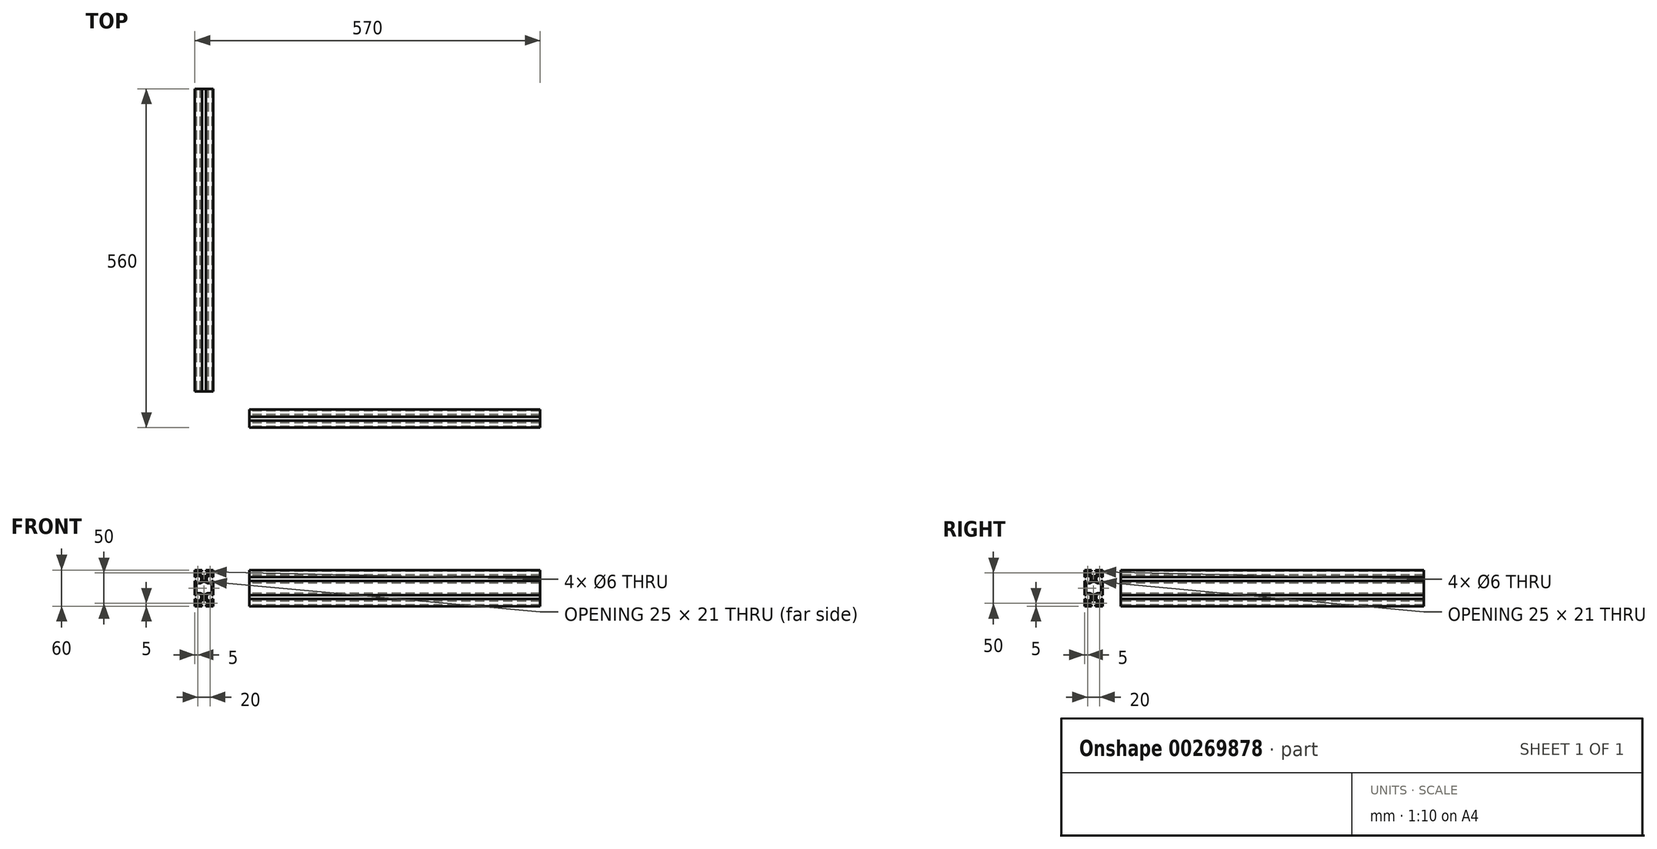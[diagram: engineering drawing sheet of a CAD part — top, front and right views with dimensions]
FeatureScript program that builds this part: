
annotation { "Feature Type Name" : "Feature", "Feature Type Description" : "" }
export const myFeature = defineFeature(function(context is Context, id is Id, definition is map)
    precondition{}
    {
        {
            var Q0;
            Q0=qCreatedBy(makeId("Top.planeOp"),FACE);
            var sketch = newSketch(context, id + "F0", { "sketchPlane" : qUnion([Q0])});
            skCircle(sketch, "E0", {"center": v(0, 0) * mm, "radius": 2.5 * mm});
            skLineSegment(sketch, "E1", {"start": v(0, 0) * mm, "end": v(-15, 0) * mm, "construction": true});
            skLineSegment(sketch, "E2", {"start": v(-15, 0) * mm, "end": v(-15, 15) * mm, "construction": true});
            skLineSegment(sketch, "E3", {"start": v(-15, 15) * mm, "end": v(0, 15) * mm, "construction": true});
            skLineSegment(sketch, "E4", {"start": v(0, 15) * mm, "end": v(0, 0) * mm, "construction": true});
            skLineSegment(sketch, "E5", {"start": v(-15, 15) * mm, "end": v(0, 0) * mm, "construction": true});
            skLineSegment(sketch, "E6", {"start": v(-15, 10) * mm, "end": v(-10, 10) * mm, "construction": true});
            skPoint(sketch, "E7", {"position": v(-15, 3.15) * mm});
            skPoint(sketch, "E8", {"position": v(-15, 5.5) * mm});
            skCircle(sketch, "E9", {"center": v(-10, 10) * mm, "radius": 3 * mm});
            skLineSegment(sketch, "E10", {"start": v(-15, 15) * mm, "end": v(-15, 3.15) * mm});
            skLineSegment(sketch, "E11", {"start": v(-15, 3.15) * mm, "end": v(-12.5, 3.15) * mm});
            skLineSegment(sketch, "E12", {"start": v(-12.5, 3.15) * mm, "end": v(-12.5, 5.5) * mm});
            skPoint(sketch, "E13", {"position": v(-4.5, 0) * mm});
            skLineSegment(sketch, "E14", {"start": v(-12.5, 5.5) * mm, "end": v(-5.5, 5.5) * mm, "construction": true});
            skArc(sketch, "E15", {"start": v(-4.5, 0) * mm, "mid": v(-5.13, 3) * mm, "end": v(-6.9, 5.5) * mm});
            skLineSegment(sketch, "E16", {"start": v(-12.5, 5.5) * mm, "end": v(-6.9, 5.5) * mm});
            skLineSegment(sketch, "E17.0.MirrorCS", {"start": v(-15, 15) * mm, "end": v(-3.15, 15) * mm});
            skPoint(sketch, "E18.visualSharp", {"position": v(-15, 15) * mm});
            skLineSegment(sketch, "E18.filletArc", {"start": v(-15, 15) * mm, "end": v(-15, 15) * mm});
            skLineSegment(sketch, "E19.0.MirrorCS", {"start": v(-3.15, 15) * mm, "end": v(-3.15, 12.5) * mm});
            skLineSegment(sketch, "E20.0.MirrorCS", {"start": v(-3.15, 12.5) * mm, "end": v(-5.5, 12.5) * mm});
            skLineSegment(sketch, "E21.0.MirrorCS", {"start": v(-5.5, 12.5) * mm, "end": v(-5.5, 6.9) * mm});
            skArc(sketch, "E22.0.MirrorCS", {"start": v(0, 4.5) * mm, "mid": v(-3, 5.13) * mm, "end": v(-5.5, 6.9) * mm});
            skArc(sketch, "E23.0.MirrorCS", {"start": v(-4.5, 0) * mm, "mid": v(-5.13, -3) * mm, "end": v(-6.9, -5.5) * mm});
            skLineSegment(sketch, "E24.0.MirrorCS", {"start": v(-12.5, -5.5) * mm, "end": v(-6.9, -5.5) * mm});
            skLineSegment(sketch, "E25.0.MirrorCS", {"start": v(-12.5, -3.15) * mm, "end": v(-12.5, -5.5) * mm});
            skLineSegment(sketch, "E26.0.MirrorCS", {"start": v(-15, -3.15) * mm, "end": v(-12.5, -3.15) * mm});
            skLineSegment(sketch, "E27.0.MirrorCS", {"start": v(-15, -15) * mm, "end": v(-15, -3.15) * mm});
            skLineSegment(sketch, "E28.0.MirrorCS", {"start": v(-15, -15) * mm, "end": v(-15, -15) * mm});
            skLineSegment(sketch, "E29.0.MirrorCS", {"start": v(-15, -15) * mm, "end": v(-3.15, -15) * mm});
            skLineSegment(sketch, "E30.0.MirrorCS", {"start": v(-3.15, -15) * mm, "end": v(-3.15, -12.5) * mm});
            skLineSegment(sketch, "E31.0.MirrorCS", {"start": v(-3.15, -12.5) * mm, "end": v(-5.5, -12.5) * mm});
            skLineSegment(sketch, "E32.0.MirrorCS", {"start": v(-5.5, -12.5) * mm, "end": v(-5.5, -6.9) * mm});
            skArc(sketch, "E33.0.MirrorCS", {"start": v(0, -4.5) * mm, "mid": v(-3, -5.13) * mm, "end": v(-5.5, -6.9) * mm});
            skCircle(sketch, "E34.0.MirrorC", {"center": v(-10, -10) * mm, "radius": 3 * mm});
            skArc(sketch, "E35.0.MirrorCS", {"start": v(0, 4.5) * mm, "mid": v(3, 5.13) * mm, "end": v(5.5, 6.9) * mm});
            skLineSegment(sketch, "E36.0.MirrorCS", {"start": v(5.5, 12.5) * mm, "end": v(5.5, 6.9) * mm});
            skLineSegment(sketch, "E37.0.MirrorCS", {"start": v(3.15, 12.5) * mm, "end": v(5.5, 12.5) * mm});
            skLineSegment(sketch, "E38.0.MirrorCS", {"start": v(3.15, 15) * mm, "end": v(3.15, 12.5) * mm});
            skArc(sketch, "E39.0.MirrorCS", {"start": v(0, -4.5) * mm, "mid": v(3, -5.13) * mm, "end": v(5.5, -6.9) * mm});
            skLineSegment(sketch, "E40.0.MirrorCS", {"start": v(5.5, -12.5) * mm, "end": v(5.5, -6.9) * mm});
            skLineSegment(sketch, "E41.0.MirrorCS", {"start": v(3.15, -12.5) * mm, "end": v(5.5, -12.5) * mm});
            skLineSegment(sketch, "E42.0.MirrorCS", {"start": v(3.15, -15) * mm, "end": v(3.15, -12.5) * mm});
            skLineSegment(sketch, "E43", {"start": v(0, 0) * mm, "end": v(30, 0) * mm, "construction": true});
            skPoint(sketch, "E44", {"position": v(15, 0) * mm});
            skLineSegment(sketch, "E45", {"start": v(15, 15) * mm, "end": v(15, -15) * mm, "construction": true});
            skCircle(sketch, "E46.0.MirrorC", {"center": v(30, 0) * mm, "radius": 2.5 * mm});
            skLineSegment(sketch, "E47.0.MirrorCS", {"start": v(26.85, 15) * mm, "end": v(26.85, 12.5) * mm});
            skLineSegment(sketch, "E48.0.MirrorCS", {"start": v(26.85, 12.5) * mm, "end": v(24.5, 12.5) * mm});
            skLineSegment(sketch, "E49.0.MirrorCS", {"start": v(24.5, 12.5) * mm, "end": v(24.5, 6.9) * mm});
            skArc(sketch, "E50.0.MirrorCS", {"start": v(30, 4.5) * mm, "mid": v(27, 5.13) * mm, "end": v(24.5, 6.9) * mm});
            skArc(sketch, "E51.0.MirrorCS", {"start": v(30, 4.5) * mm, "mid": v(33, 5.13) * mm, "end": v(35.5, 6.9) * mm});
            skLineSegment(sketch, "E52.0.MirrorCS", {"start": v(35.5, 12.5) * mm, "end": v(35.5, 6.9) * mm});
            skLineSegment(sketch, "E53.0.MirrorCS", {"start": v(33.15, 12.5) * mm, "end": v(35.5, 12.5) * mm});
            skLineSegment(sketch, "E54.0.MirrorCS", {"start": v(33.15, 15) * mm, "end": v(33.15, 12.5) * mm});
            skLineSegment(sketch, "E55.0.MirrorCS", {"start": v(45, 15) * mm, "end": v(33.15, 15) * mm});
            skLineSegment(sketch, "E56.0.MirrorCS", {"start": v(45, 15) * mm, "end": v(45, 15) * mm});
            skLineSegment(sketch, "E57.0.MirrorCS", {"start": v(45, 15) * mm, "end": v(45, 3.15) * mm});
            skLineSegment(sketch, "E58.0.MirrorCS", {"start": v(45, 3.15) * mm, "end": v(42.5, 3.15) * mm});
            skLineSegment(sketch, "E59.0.MirrorCS", {"start": v(42.5, 3.15) * mm, "end": v(42.5, 5.5) * mm});
            skLineSegment(sketch, "E60.0.MirrorCS", {"start": v(42.5, 5.5) * mm, "end": v(36.9, 5.5) * mm});
            skArc(sketch, "E61.0.MirrorCS", {"start": v(34.5, 0) * mm, "mid": v(35.13, 3) * mm, "end": v(36.9, 5.5) * mm});
            skArc(sketch, "E62.0.MirrorCS", {"start": v(34.5, 0) * mm, "mid": v(35.13, -3) * mm, "end": v(36.9, -5.5) * mm});
            skLineSegment(sketch, "E63.0.MirrorCS", {"start": v(42.5, -5.5) * mm, "end": v(36.9, -5.5) * mm});
            skLineSegment(sketch, "E64.0.MirrorCS", {"start": v(42.5, -3.15) * mm, "end": v(42.5, -5.5) * mm});
            skLineSegment(sketch, "E65.0.MirrorCS", {"start": v(45, -3.15) * mm, "end": v(42.5, -3.15) * mm});
            skLineSegment(sketch, "E66.0.MirrorCS", {"start": v(45, -15) * mm, "end": v(45, -3.15) * mm});
            skLineSegment(sketch, "E67.0.MirrorCS", {"start": v(45, -15) * mm, "end": v(45, -15) * mm});
            skLineSegment(sketch, "E68.0.MirrorCS", {"start": v(45, -15) * mm, "end": v(33.15, -15) * mm});
            skLineSegment(sketch, "E69.0.MirrorCS", {"start": v(33.15, -15) * mm, "end": v(33.15, -12.5) * mm});
            skLineSegment(sketch, "E70.0.MirrorCS", {"start": v(33.15, -12.5) * mm, "end": v(35.5, -12.5) * mm});
            skLineSegment(sketch, "E71.0.MirrorCS", {"start": v(35.5, -12.5) * mm, "end": v(35.5, -6.9) * mm});
            skArc(sketch, "E72.0.MirrorCS", {"start": v(30, -4.5) * mm, "mid": v(33, -5.13) * mm, "end": v(35.5, -6.9) * mm});
            skArc(sketch, "E73.0.MirrorCS", {"start": v(30, -4.5) * mm, "mid": v(27, -5.13) * mm, "end": v(24.5, -6.9) * mm});
            skLineSegment(sketch, "E74.0.MirrorCS", {"start": v(24.5, -12.5) * mm, "end": v(24.5, -6.9) * mm});
            skLineSegment(sketch, "E75.0.MirrorCS", {"start": v(26.85, -12.5) * mm, "end": v(24.5, -12.5) * mm});
            skLineSegment(sketch, "E76.0.MirrorCS", {"start": v(26.85, -15) * mm, "end": v(26.85, -12.5) * mm});
            skCircle(sketch, "E77.0.MirrorC", {"center": v(40, -10) * mm, "radius": 3 * mm});
            skCircle(sketch, "E78.0.MirrorC", {"center": v(40, 10) * mm, "radius": 3 * mm});
            skLineSegment(sketch, "E79", {"start": v(3.15, 15) * mm, "end": v(26.85, 15) * mm});
            skLineSegment(sketch, "E80", {"start": v(3.15, -15) * mm, "end": v(26.85, -15) * mm});
            skLineSegment(sketch, "E81.0.MirrorCS", {"start": v(0, 15) * mm, "end": v(0, 30) * mm, "construction": true});
            skArc(sketch, "E82.0.MirrorCS", {"start": v(4.5, 0) * mm, "mid": v(5.05, 2.82) * mm, "end": v(6.62, 5.22) * mm});
            skLineSegment(sketch, "E83", {"start": v(6.9, 5.92) * mm, "end": v(6.9, 11.5) * mm});
            skLineSegment(sketch, "E84", {"start": v(7.9, 12.5) * mm, "end": v(15, 12.5) * mm});
            skPoint(sketch, "E85.visualSharp", {"position": v(6.9, 5.5) * mm});
            skArc(sketch, "E85.filletArc", {"start": v(6.62, 5.22) * mm, "mid": v(6.83, 5.54) * mm, "end": v(6.9, 5.92) * mm});
            skPoint(sketch, "E86.visualSharp", {"position": v(6.9, 12.5) * mm});
            skArc(sketch, "E86.filletArc", {"start": v(7.9, 12.5) * mm, "mid": v(7.2, 12.2) * mm, "end": v(6.9, 11.5) * mm});
            skPoint(sketch, "E87", {"position": v(15, 12.5) * mm});
            skLineSegment(sketch, "E88.0.MirrorCS", {"start": v(22.1, 12.5) * mm, "end": v(15, 12.5) * mm});
            skArc(sketch, "E89.0.MirrorCS", {"start": v(22.1, 12.5) * mm, "mid": v(22.8, 12.2) * mm, "end": v(23.1, 11.5) * mm});
            skLineSegment(sketch, "E90.0.MirrorCS", {"start": v(23.1, 5.92) * mm, "end": v(23.1, 11.5) * mm});
            skArc(sketch, "E91.0.MirrorCS", {"start": v(23.38, 5.22) * mm, "mid": v(23.17, 5.54) * mm, "end": v(23.1, 5.92) * mm});
            skArc(sketch, "E92.0.MirrorCS", {"start": v(25.5, 0) * mm, "mid": v(24.95, 2.82) * mm, "end": v(23.38, 5.22) * mm});
            skArc(sketch, "E93.0.MirrorCS", {"start": v(4.5, 0) * mm, "mid": v(5.05, -2.82) * mm, "end": v(6.62, -5.22) * mm});
            skPoint(sketch, "E94.0.MirrorP", {"position": v(6.9, -5.5) * mm});
            skArc(sketch, "E95.0.MirrorCS", {"start": v(6.62, -5.22) * mm, "mid": v(6.83, -5.54) * mm, "end": v(6.9, -5.92) * mm});
            skLineSegment(sketch, "E96.0.MirrorCS", {"start": v(6.9, -5.92) * mm, "end": v(6.9, -11.5) * mm});
            skLineSegment(sketch, "E97.0.MirrorCS", {"start": v(7.9, -12.5) * mm, "end": v(15, -12.5) * mm});
            skArc(sketch, "E98.0.MirrorCS", {"start": v(7.9, -12.5) * mm, "mid": v(7.2, -12.2) * mm, "end": v(6.9, -11.5) * mm});
            skLineSegment(sketch, "E99.0.MirrorCS", {"start": v(22.1, -12.5) * mm, "end": v(15, -12.5) * mm});
            skArc(sketch, "E100.0.MirrorCS", {"start": v(22.1, -12.5) * mm, "mid": v(22.8, -12.2) * mm, "end": v(23.1, -11.5) * mm});
            skLineSegment(sketch, "E101.0.MirrorCS", {"start": v(23.1, -5.92) * mm, "end": v(23.1, -11.5) * mm});
            skArc(sketch, "E102.0.MirrorCS", {"start": v(23.38, -5.22) * mm, "mid": v(23.17, -5.54) * mm, "end": v(23.1, -5.92) * mm});
            skArc(sketch, "E103.0.MirrorCS", {"start": v(25.5, 0) * mm, "mid": v(24.95, -2.82) * mm, "end": v(23.38, -5.22) * mm});
            skSolve(sketch);
        }
        {
            var Q0;
            Q0=qSketchRegion(id+"F0",true);
            extrude(context, id + "F1", {"entities" : qUnion([Q0]), "depth" : 500 * mm});
        }
        {
            var Q0;
            Q0=qSketchRegion(id+"F0",true);
            extrude(context, id + "F2", {"entities" : qUnion([Q0]), "depth" : 480 * mm});
        }
        {
            var Q0;
            Q0=makeQuery(id+"F2.opExtrude","SWEPT_BODY",BODY,{"disambiguationData":[OSD([sQuery(id+"F0.wireOp",EDGE,"E0"),sQuery(id+"F0.wireOp",EDGE,"E9"),sQuery(id+"F0.wireOp",EDGE,"E10"),sQuery(id+"F0.wireOp",EDGE,"E11"),sQuery(id+"F0.wireOp",EDGE,"E12"),sQuery(id+"F0.wireOp",EDGE,"E15"),sQuery(id+"F0.wireOp",EDGE,"E16"),sQuery(id+"F0.wireOp",EDGE,"E17.0.MirrorCS"),sQuery(id+"F0.wireOp",EDGE,"E19.0.MirrorCS"),sQuery(id+"F0.wireOp",EDGE,"E20.0.MirrorCS"),sQuery(id+"F0.wireOp",EDGE,"E21.0.MirrorCS"),sQuery(id+"F0.wireOp",EDGE,"E22.0.MirrorCS"),sQuery(id+"F0.wireOp",EDGE,"E23.0.MirrorCS"),sQuery(id+"F0.wireOp",EDGE,"E24.0.MirrorCS"),sQuery(id+"F0.wireOp",EDGE,"E25.0.MirrorCS"),sQuery(id+"F0.wireOp",EDGE,"E26.0.MirrorCS"),sQuery(id+"F0.wireOp",EDGE,"E27.0.MirrorCS"),sQuery(id+"F0.wireOp",EDGE,"E29.0.MirrorCS"),sQuery(id+"F0.wireOp",EDGE,"E30.0.MirrorCS"),sQuery(id+"F0.wireOp",EDGE,"E31.0.MirrorCS"),sQuery(id+"F0.wireOp",EDGE,"E32.0.MirrorCS"),sQuery(id+"F0.wireOp",EDGE,"E33.0.MirrorCS"),sQuery(id+"F0.wireOp",EDGE,"E34.0.MirrorC"),sQuery(id+"F0.wireOp",EDGE,"E35.0.MirrorCS"),sQuery(id+"F0.wireOp",EDGE,"E36.0.MirrorCS"),sQuery(id+"F0.wireOp",EDGE,"E37.0.MirrorCS"),sQuery(id+"F0.wireOp",EDGE,"E38.0.MirrorCS"),sQuery(id+"F0.wireOp",EDGE,"E39.0.MirrorCS"),sQuery(id+"F0.wireOp",EDGE,"E40.0.MirrorCS"),sQuery(id+"F0.wireOp",EDGE,"E41.0.MirrorCS"),sQuery(id+"F0.wireOp",EDGE,"E42.0.MirrorCS"),sQuery(id+"F0.wireOp",EDGE,"E46.0.MirrorC"),sQuery(id+"F0.wireOp",EDGE,"E47.0.MirrorCS"),sQuery(id+"F0.wireOp",EDGE,"E48.0.MirrorCS"),sQuery(id+"F0.wireOp",EDGE,"E49.0.MirrorCS"),sQuery(id+"F0.wireOp",EDGE,"E50.0.MirrorCS"),sQuery(id+"F0.wireOp",EDGE,"E51.0.MirrorCS"),sQuery(id+"F0.wireOp",EDGE,"E52.0.MirrorCS"),sQuery(id+"F0.wireOp",EDGE,"E53.0.MirrorCS"),sQuery(id+"F0.wireOp",EDGE,"E54.0.MirrorCS"),sQuery(id+"F0.wireOp",EDGE,"E55.0.MirrorCS"),sQuery(id+"F0.wireOp",EDGE,"E57.0.MirrorCS"),sQuery(id+"F0.wireOp",EDGE,"E58.0.MirrorCS"),sQuery(id+"F0.wireOp",EDGE,"E59.0.MirrorCS"),sQuery(id+"F0.wireOp",EDGE,"E60.0.MirrorCS"),sQuery(id+"F0.wireOp",EDGE,"E61.0.MirrorCS"),sQuery(id+"F0.wireOp",EDGE,"E62.0.MirrorCS"),sQuery(id+"F0.wireOp",EDGE,"E63.0.MirrorCS"),sQuery(id+"F0.wireOp",EDGE,"E64.0.MirrorCS"),sQuery(id+"F0.wireOp",EDGE,"E65.0.MirrorCS"),sQuery(id+"F0.wireOp",EDGE,"E66.0.MirrorCS"),sQuery(id+"F0.wireOp",EDGE,"E68.0.MirrorCS"),sQuery(id+"F0.wireOp",EDGE,"E69.0.MirrorCS"),sQuery(id+"F0.wireOp",EDGE,"E70.0.MirrorCS"),sQuery(id+"F0.wireOp",EDGE,"E71.0.MirrorCS"),sQuery(id+"F0.wireOp",EDGE,"E72.0.MirrorCS"),sQuery(id+"F0.wireOp",EDGE,"E73.0.MirrorCS"),sQuery(id+"F0.wireOp",EDGE,"E74.0.MirrorCS"),sQuery(id+"F0.wireOp",EDGE,"E75.0.MirrorCS"),sQuery(id+"F0.wireOp",EDGE,"E76.0.MirrorCS"),sQuery(id+"F0.wireOp",EDGE,"E77.0.MirrorC"),sQuery(id+"F0.wireOp",EDGE,"E78.0.MirrorC"),sQuery(id+"F0.wireOp",EDGE,"E79"),sQuery(id+"F0.wireOp",EDGE,"E80"),sQuery(id+"F0.wireOp",EDGE,"E82.0.MirrorCS"),sQuery(id+"F0.wireOp",EDGE,"E83"),sQuery(id+"F0.wireOp",EDGE,"E84"),sQuery(id+"F0.wireOp",EDGE,"E85.filletArc"),sQuery(id+"F0.wireOp",EDGE,"E86.filletArc"),sQuery(id+"F0.wireOp",EDGE,"E88.0.MirrorCS"),sQuery(id+"F0.wireOp",EDGE,"E89.0.MirrorCS"),sQuery(id+"F0.wireOp",EDGE,"E90.0.MirrorCS"),sQuery(id+"F0.wireOp",EDGE,"E91.0.MirrorCS"),sQuery(id+"F0.wireOp",EDGE,"E92.0.MirrorCS"),sQuery(id+"F0.wireOp",EDGE,"E93.0.MirrorCS"),sQuery(id+"F0.wireOp",EDGE,"E95.0.MirrorCS"),sQuery(id+"F0.wireOp",EDGE,"E96.0.MirrorCS"),sQuery(id+"F0.wireOp",EDGE,"E97.0.MirrorCS"),sQuery(id+"F0.wireOp",EDGE,"E98.0.MirrorCS"),sQuery(id+"F0.wireOp",EDGE,"E99.0.MirrorCS"),sQuery(id+"F0.wireOp",EDGE,"E100.0.MirrorCS"),sQuery(id+"F0.wireOp",EDGE,"E101.0.MirrorCS"),sQuery(id+"F0.wireOp",EDGE,"E102.0.MirrorCS"),sQuery(id+"F0.wireOp",EDGE,"E103.0.MirrorCS")])]});
            var Q1;
            Q1=makeQuery(id+"F1.opExtrude","CAP_EDGE",EDGE,{"disambiguationData":[OSD([sQuery(id+"F0.wireOp",EDGE,"E66.0.MirrorCS")])],"isStart":true});
            transform(context, id + "F3", {"entities" : qUnion([Q0]), "transformType" : TransformType.ROTATION, "transformAxis" : qUnion([Q1]), "angle" : 90 * degree, "makeCopy" : false});
        }
        {
            var Q0;
            Q0=makeQuery(id+"F1.opExtrude","SWEPT_BODY",BODY,{"disambiguationData":[OSD([sQuery(id+"F0.wireOp",EDGE,"E0"),sQuery(id+"F0.wireOp",EDGE,"E9"),sQuery(id+"F0.wireOp",EDGE,"E10"),sQuery(id+"F0.wireOp",EDGE,"E11"),sQuery(id+"F0.wireOp",EDGE,"E12"),sQuery(id+"F0.wireOp",EDGE,"E15"),sQuery(id+"F0.wireOp",EDGE,"E16"),sQuery(id+"F0.wireOp",EDGE,"E17.0.MirrorCS"),sQuery(id+"F0.wireOp",EDGE,"E19.0.MirrorCS"),sQuery(id+"F0.wireOp",EDGE,"E20.0.MirrorCS"),sQuery(id+"F0.wireOp",EDGE,"E21.0.MirrorCS"),sQuery(id+"F0.wireOp",EDGE,"E22.0.MirrorCS"),sQuery(id+"F0.wireOp",EDGE,"E23.0.MirrorCS"),sQuery(id+"F0.wireOp",EDGE,"E24.0.MirrorCS"),sQuery(id+"F0.wireOp",EDGE,"E25.0.MirrorCS"),sQuery(id+"F0.wireOp",EDGE,"E26.0.MirrorCS"),sQuery(id+"F0.wireOp",EDGE,"E27.0.MirrorCS"),sQuery(id+"F0.wireOp",EDGE,"E29.0.MirrorCS"),sQuery(id+"F0.wireOp",EDGE,"E30.0.MirrorCS"),sQuery(id+"F0.wireOp",EDGE,"E31.0.MirrorCS"),sQuery(id+"F0.wireOp",EDGE,"E32.0.MirrorCS"),sQuery(id+"F0.wireOp",EDGE,"E33.0.MirrorCS"),sQuery(id+"F0.wireOp",EDGE,"E34.0.MirrorC"),sQuery(id+"F0.wireOp",EDGE,"E35.0.MirrorCS"),sQuery(id+"F0.wireOp",EDGE,"E36.0.MirrorCS"),sQuery(id+"F0.wireOp",EDGE,"E37.0.MirrorCS"),sQuery(id+"F0.wireOp",EDGE,"E38.0.MirrorCS"),sQuery(id+"F0.wireOp",EDGE,"E39.0.MirrorCS"),sQuery(id+"F0.wireOp",EDGE,"E40.0.MirrorCS"),sQuery(id+"F0.wireOp",EDGE,"E41.0.MirrorCS"),sQuery(id+"F0.wireOp",EDGE,"E42.0.MirrorCS"),sQuery(id+"F0.wireOp",EDGE,"E46.0.MirrorC"),sQuery(id+"F0.wireOp",EDGE,"E47.0.MirrorCS"),sQuery(id+"F0.wireOp",EDGE,"E48.0.MirrorCS"),sQuery(id+"F0.wireOp",EDGE,"E49.0.MirrorCS"),sQuery(id+"F0.wireOp",EDGE,"E50.0.MirrorCS"),sQuery(id+"F0.wireOp",EDGE,"E51.0.MirrorCS"),sQuery(id+"F0.wireOp",EDGE,"E52.0.MirrorCS"),sQuery(id+"F0.wireOp",EDGE,"E53.0.MirrorCS"),sQuery(id+"F0.wireOp",EDGE,"E54.0.MirrorCS"),sQuery(id+"F0.wireOp",EDGE,"E55.0.MirrorCS"),sQuery(id+"F0.wireOp",EDGE,"E57.0.MirrorCS"),sQuery(id+"F0.wireOp",EDGE,"E58.0.MirrorCS"),sQuery(id+"F0.wireOp",EDGE,"E59.0.MirrorCS"),sQuery(id+"F0.wireOp",EDGE,"E60.0.MirrorCS"),sQuery(id+"F0.wireOp",EDGE,"E61.0.MirrorCS"),sQuery(id+"F0.wireOp",EDGE,"E62.0.MirrorCS"),sQuery(id+"F0.wireOp",EDGE,"E63.0.MirrorCS"),sQuery(id+"F0.wireOp",EDGE,"E64.0.MirrorCS"),sQuery(id+"F0.wireOp",EDGE,"E65.0.MirrorCS"),sQuery(id+"F0.wireOp",EDGE,"E66.0.MirrorCS"),sQuery(id+"F0.wireOp",EDGE,"E68.0.MirrorCS"),sQuery(id+"F0.wireOp",EDGE,"E69.0.MirrorCS"),sQuery(id+"F0.wireOp",EDGE,"E70.0.MirrorCS"),sQuery(id+"F0.wireOp",EDGE,"E71.0.MirrorCS"),sQuery(id+"F0.wireOp",EDGE,"E72.0.MirrorCS"),sQuery(id+"F0.wireOp",EDGE,"E73.0.MirrorCS"),sQuery(id+"F0.wireOp",EDGE,"E74.0.MirrorCS"),sQuery(id+"F0.wireOp",EDGE,"E75.0.MirrorCS"),sQuery(id+"F0.wireOp",EDGE,"E76.0.MirrorCS"),sQuery(id+"F0.wireOp",EDGE,"E77.0.MirrorC"),sQuery(id+"F0.wireOp",EDGE,"E78.0.MirrorC"),sQuery(id+"F0.wireOp",EDGE,"E79"),sQuery(id+"F0.wireOp",EDGE,"E80"),sQuery(id+"F0.wireOp",EDGE,"E82.0.MirrorCS"),sQuery(id+"F0.wireOp",EDGE,"E83"),sQuery(id+"F0.wireOp",EDGE,"E84"),sQuery(id+"F0.wireOp",EDGE,"E85.filletArc"),sQuery(id+"F0.wireOp",EDGE,"E86.filletArc"),sQuery(id+"F0.wireOp",EDGE,"E88.0.MirrorCS"),sQuery(id+"F0.wireOp",EDGE,"E89.0.MirrorCS"),sQuery(id+"F0.wireOp",EDGE,"E90.0.MirrorCS"),sQuery(id+"F0.wireOp",EDGE,"E91.0.MirrorCS"),sQuery(id+"F0.wireOp",EDGE,"E92.0.MirrorCS"),sQuery(id+"F0.wireOp",EDGE,"E93.0.MirrorCS"),sQuery(id+"F0.wireOp",EDGE,"E95.0.MirrorCS"),sQuery(id+"F0.wireOp",EDGE,"E96.0.MirrorCS"),sQuery(id+"F0.wireOp",EDGE,"E97.0.MirrorCS"),sQuery(id+"F0.wireOp",EDGE,"E98.0.MirrorCS"),sQuery(id+"F0.wireOp",EDGE,"E99.0.MirrorCS"),sQuery(id+"F0.wireOp",EDGE,"E100.0.MirrorCS"),sQuery(id+"F0.wireOp",EDGE,"E101.0.MirrorCS"),sQuery(id+"F0.wireOp",EDGE,"E102.0.MirrorCS"),sQuery(id+"F0.wireOp",EDGE,"E103.0.MirrorCS")])]});
            var Q1;
            Q1=makeQuery(id+"F1.opExtrude","SWEPT_EDGE",EDGE,{"disambiguationData":[OSD([sQuery(id+"F0.wireOp",EDGE,"E27.0.MirrorCS"),sQuery(id+"F0.wireOp",EDGE,"E29.0.MirrorCS")])]});
            transform(context, id + "F4", {"entities" : qUnion([Q0]), "transformType" : TransformType.ROTATION, "transformAxis" : qUnion([Q1]), "angle" : 270 * degree, "makeCopy" : false});
        }
        {
            var Q0;
            Q0=makeQuery(id+"F1.opExtrude","SWEPT_BODY",BODY,{"disambiguationData":[OSD([sQuery(id+"F0.wireOp",EDGE,"E0"),sQuery(id+"F0.wireOp",EDGE,"E9"),sQuery(id+"F0.wireOp",EDGE,"E10"),sQuery(id+"F0.wireOp",EDGE,"E11"),sQuery(id+"F0.wireOp",EDGE,"E12"),sQuery(id+"F0.wireOp",EDGE,"E15"),sQuery(id+"F0.wireOp",EDGE,"E16"),sQuery(id+"F0.wireOp",EDGE,"E17.0.MirrorCS"),sQuery(id+"F0.wireOp",EDGE,"E19.0.MirrorCS"),sQuery(id+"F0.wireOp",EDGE,"E20.0.MirrorCS"),sQuery(id+"F0.wireOp",EDGE,"E21.0.MirrorCS"),sQuery(id+"F0.wireOp",EDGE,"E22.0.MirrorCS"),sQuery(id+"F0.wireOp",EDGE,"E23.0.MirrorCS"),sQuery(id+"F0.wireOp",EDGE,"E24.0.MirrorCS"),sQuery(id+"F0.wireOp",EDGE,"E25.0.MirrorCS"),sQuery(id+"F0.wireOp",EDGE,"E26.0.MirrorCS"),sQuery(id+"F0.wireOp",EDGE,"E27.0.MirrorCS"),sQuery(id+"F0.wireOp",EDGE,"E29.0.MirrorCS"),sQuery(id+"F0.wireOp",EDGE,"E30.0.MirrorCS"),sQuery(id+"F0.wireOp",EDGE,"E31.0.MirrorCS"),sQuery(id+"F0.wireOp",EDGE,"E32.0.MirrorCS"),sQuery(id+"F0.wireOp",EDGE,"E33.0.MirrorCS"),sQuery(id+"F0.wireOp",EDGE,"E34.0.MirrorC"),sQuery(id+"F0.wireOp",EDGE,"E35.0.MirrorCS"),sQuery(id+"F0.wireOp",EDGE,"E36.0.MirrorCS"),sQuery(id+"F0.wireOp",EDGE,"E37.0.MirrorCS"),sQuery(id+"F0.wireOp",EDGE,"E38.0.MirrorCS"),sQuery(id+"F0.wireOp",EDGE,"E39.0.MirrorCS"),sQuery(id+"F0.wireOp",EDGE,"E40.0.MirrorCS"),sQuery(id+"F0.wireOp",EDGE,"E41.0.MirrorCS"),sQuery(id+"F0.wireOp",EDGE,"E42.0.MirrorCS"),sQuery(id+"F0.wireOp",EDGE,"E46.0.MirrorC"),sQuery(id+"F0.wireOp",EDGE,"E47.0.MirrorCS"),sQuery(id+"F0.wireOp",EDGE,"E48.0.MirrorCS"),sQuery(id+"F0.wireOp",EDGE,"E49.0.MirrorCS"),sQuery(id+"F0.wireOp",EDGE,"E50.0.MirrorCS"),sQuery(id+"F0.wireOp",EDGE,"E51.0.MirrorCS"),sQuery(id+"F0.wireOp",EDGE,"E52.0.MirrorCS"),sQuery(id+"F0.wireOp",EDGE,"E53.0.MirrorCS"),sQuery(id+"F0.wireOp",EDGE,"E54.0.MirrorCS"),sQuery(id+"F0.wireOp",EDGE,"E55.0.MirrorCS"),sQuery(id+"F0.wireOp",EDGE,"E57.0.MirrorCS"),sQuery(id+"F0.wireOp",EDGE,"E58.0.MirrorCS"),sQuery(id+"F0.wireOp",EDGE,"E59.0.MirrorCS"),sQuery(id+"F0.wireOp",EDGE,"E60.0.MirrorCS"),sQuery(id+"F0.wireOp",EDGE,"E61.0.MirrorCS"),sQuery(id+"F0.wireOp",EDGE,"E62.0.MirrorCS"),sQuery(id+"F0.wireOp",EDGE,"E63.0.MirrorCS"),sQuery(id+"F0.wireOp",EDGE,"E64.0.MirrorCS"),sQuery(id+"F0.wireOp",EDGE,"E65.0.MirrorCS"),sQuery(id+"F0.wireOp",EDGE,"E66.0.MirrorCS"),sQuery(id+"F0.wireOp",EDGE,"E68.0.MirrorCS"),sQuery(id+"F0.wireOp",EDGE,"E69.0.MirrorCS"),sQuery(id+"F0.wireOp",EDGE,"E70.0.MirrorCS"),sQuery(id+"F0.wireOp",EDGE,"E71.0.MirrorCS"),sQuery(id+"F0.wireOp",EDGE,"E72.0.MirrorCS"),sQuery(id+"F0.wireOp",EDGE,"E73.0.MirrorCS"),sQuery(id+"F0.wireOp",EDGE,"E74.0.MirrorCS"),sQuery(id+"F0.wireOp",EDGE,"E75.0.MirrorCS"),sQuery(id+"F0.wireOp",EDGE,"E76.0.MirrorCS"),sQuery(id+"F0.wireOp",EDGE,"E77.0.MirrorC"),sQuery(id+"F0.wireOp",EDGE,"E78.0.MirrorC"),sQuery(id+"F0.wireOp",EDGE,"E79"),sQuery(id+"F0.wireOp",EDGE,"E80"),sQuery(id+"F0.wireOp",EDGE,"E82.0.MirrorCS"),sQuery(id+"F0.wireOp",EDGE,"E83"),sQuery(id+"F0.wireOp",EDGE,"E84"),sQuery(id+"F0.wireOp",EDGE,"E85.filletArc"),sQuery(id+"F0.wireOp",EDGE,"E86.filletArc"),sQuery(id+"F0.wireOp",EDGE,"E88.0.MirrorCS"),sQuery(id+"F0.wireOp",EDGE,"E89.0.MirrorCS"),sQuery(id+"F0.wireOp",EDGE,"E90.0.MirrorCS"),sQuery(id+"F0.wireOp",EDGE,"E91.0.MirrorCS"),sQuery(id+"F0.wireOp",EDGE,"E92.0.MirrorCS"),sQuery(id+"F0.wireOp",EDGE,"E93.0.MirrorCS"),sQuery(id+"F0.wireOp",EDGE,"E95.0.MirrorCS"),sQuery(id+"F0.wireOp",EDGE,"E96.0.MirrorCS"),sQuery(id+"F0.wireOp",EDGE,"E97.0.MirrorCS"),sQuery(id+"F0.wireOp",EDGE,"E98.0.MirrorCS"),sQuery(id+"F0.wireOp",EDGE,"E99.0.MirrorCS"),sQuery(id+"F0.wireOp",EDGE,"E100.0.MirrorCS"),sQuery(id+"F0.wireOp",EDGE,"E101.0.MirrorCS"),sQuery(id+"F0.wireOp",EDGE,"E102.0.MirrorCS"),sQuery(id+"F0.wireOp",EDGE,"E103.0.MirrorCS")])]});
            var Q1;
            Q1=makeQuery(id+"F1.opExtrude","CAP_EDGE",EDGE,{"disambiguationData":[OSD([sQuery(id+"F0.wireOp",EDGE,"E66.0.MirrorCS")])],"isStart":true});
            transform(context, id + "F5", {"entities" : qUnion([Q0]), "transformType" : TransformType.ROTATION, "transformAxis" : qUnion([Q1]), "angle" : 90 * degree, "makeCopy" : false});
        }
    });
